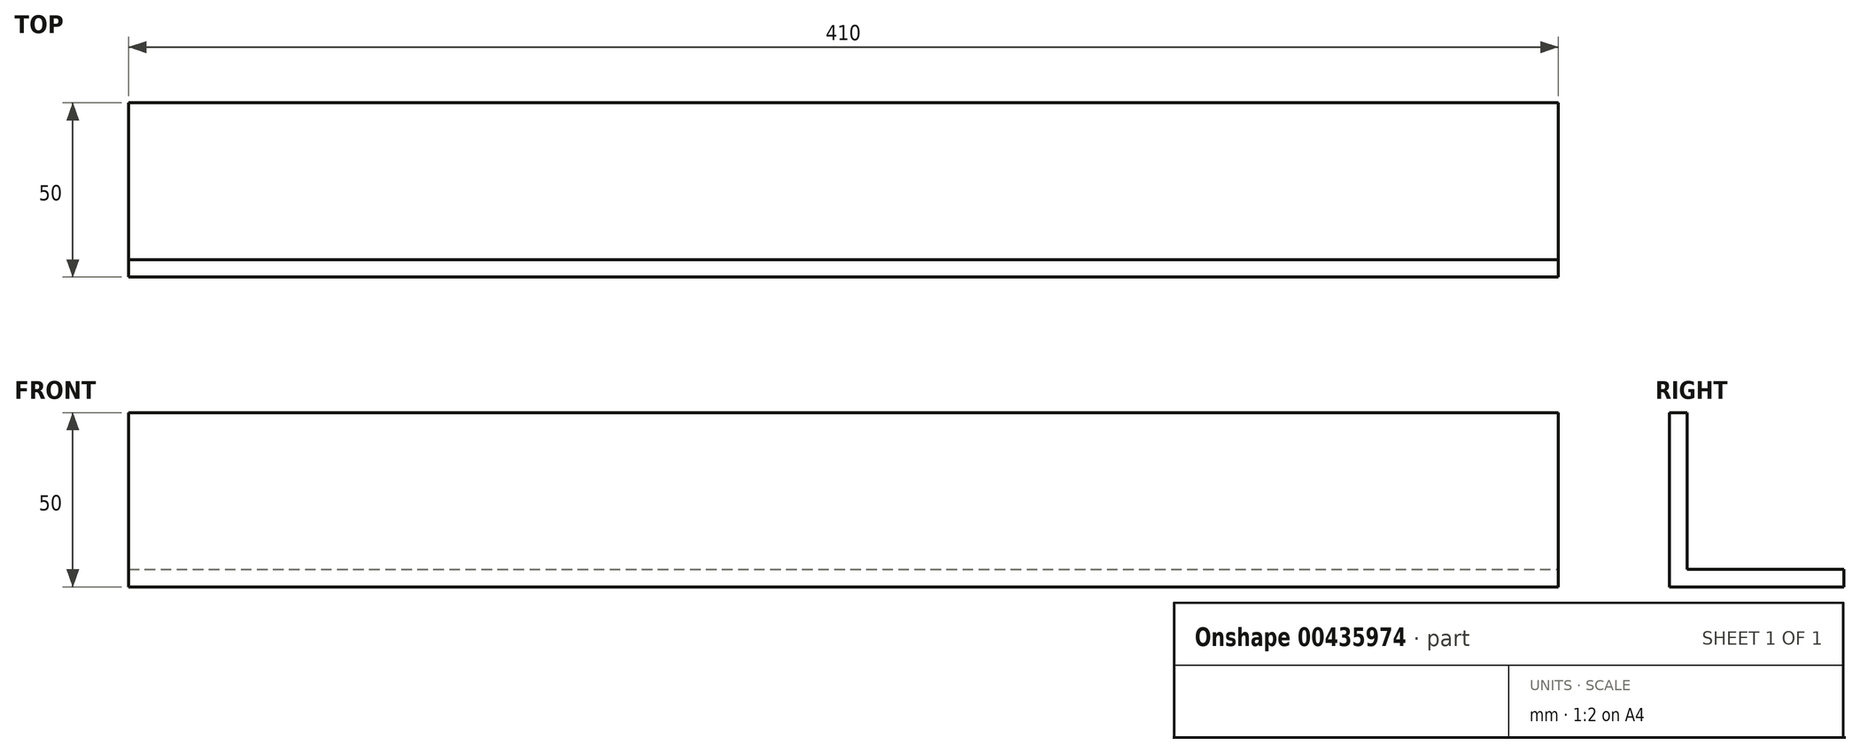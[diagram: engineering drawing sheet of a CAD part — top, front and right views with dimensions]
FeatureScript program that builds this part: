
annotation { "Feature Type Name" : "Feature", "Feature Type Description" : "" }
export const myFeature = defineFeature(function(context is Context, id is Id, definition is map)
    precondition{}
    {
        {
            var Q0;
            Q0=qCreatedBy(makeId("Right.planeOp"),FACE);
            var sketch = newSketch(context, id + "F0", { "sketchPlane" : qUnion([Q0])});
            skLineSegment(sketch, "E0.bottom", {"start": v(0, 0) * mm, "end": v(-50, 0) * mm});
            skLineSegment(sketch, "E0.right", {"start": v(-50, 0) * mm, "end": v(-50, 50) * mm});
            skLineSegment(sketch, "E1.0", {"start": v(0, 5) * mm, "end": v(-45, 5) * mm});
            skLineSegment(sketch, "E2.0", {"start": v(-45, 5) * mm, "end": v(-45, 50) * mm});
            skLineSegment(sketch, "E3", {"start": v(-50, 50) * mm, "end": v(-45, 50) * mm});
            skLineSegment(sketch, "E4", {"start": v(0, 5) * mm, "end": v(0, 0) * mm});
            skSolve(sketch);
        }
        {
            var Q0;
            Q0=qSketchRegion(id+"F0",true);
            extrude(context, id + "F1", {"entities" : qUnion([Q0]), "oppositeDirection" : true, "depth" : 410 * mm});
        }
    });
